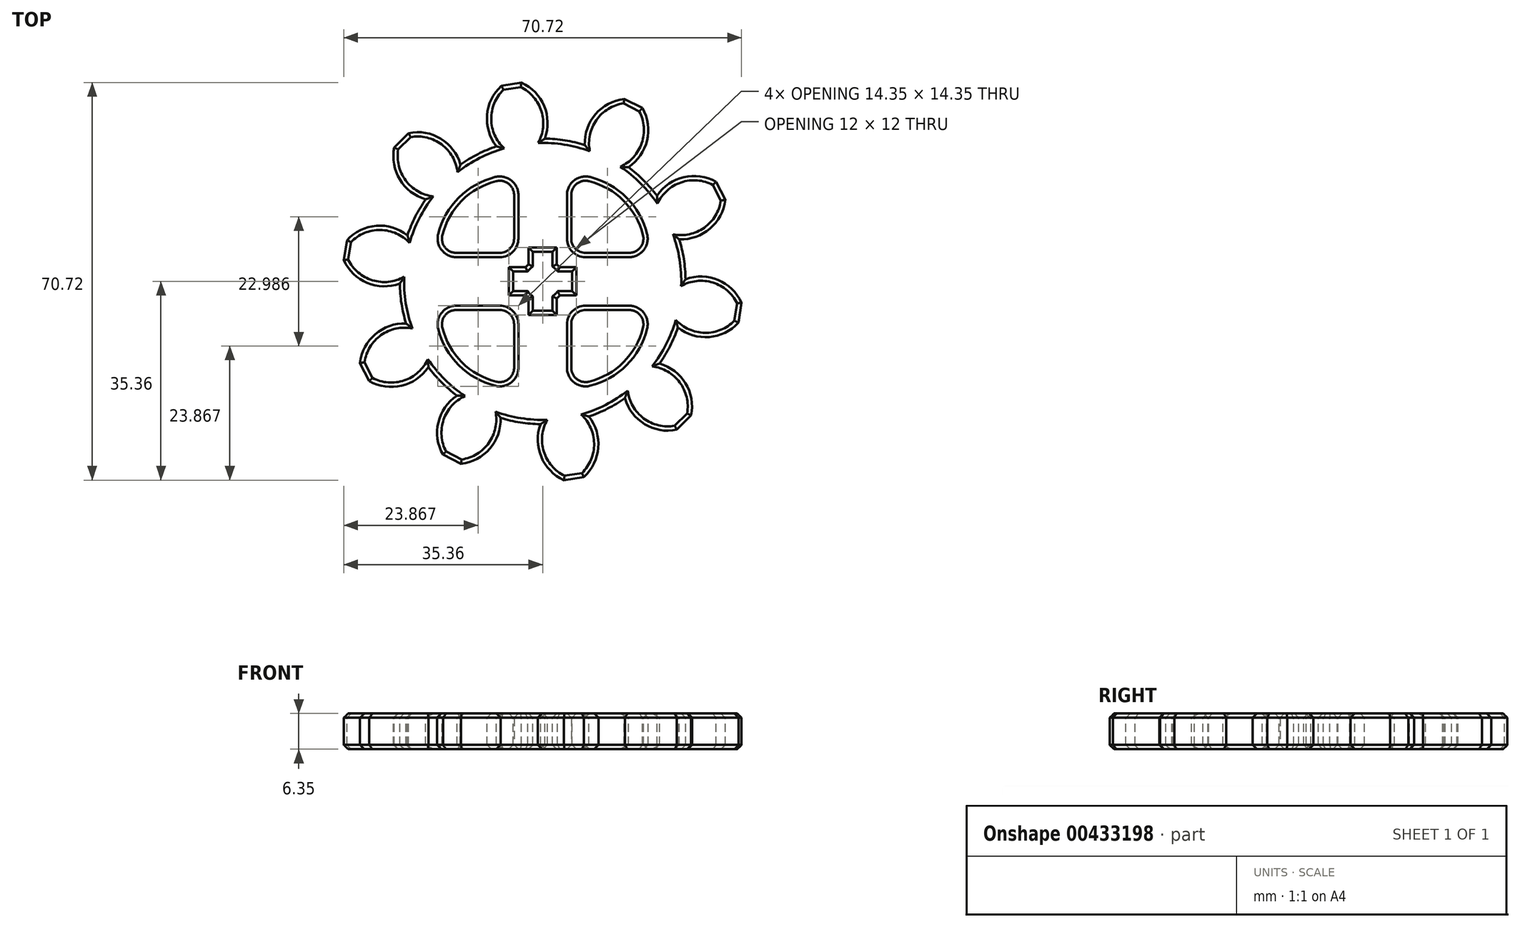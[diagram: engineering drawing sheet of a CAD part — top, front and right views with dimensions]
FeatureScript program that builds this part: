
annotation { "Feature Type Name" : "Feature", "Feature Type Description" : "" }
export const myFeature = defineFeature(function(context is Context, id is Id, definition is map)
    precondition{}
    {
        {
            var Q0;
            Q0=qCreatedBy(makeId("Top.planeOp"),FACE);
            var sketch = newSketch(context, id + "F0", { "sketchPlane" : qUnion([Q0])});
            skCircle(sketch, "E0", {"center": v(0, 0) * mm, "radius": 30.48 * mm, "construction": true});
            skSolve(sketch);
        }
        {
            var Q0;
            Q0=qCreatedBy(makeId("Top.planeOp"),FACE);
            var sketch = newSketch(context, id + "F1", { "sketchPlane" : qUnion([Q0])});
            skCircle(sketch, "E1", {"center": v(0, 0) * mm, "radius": 35.56 * mm, "construction": true});
            skCircle(sketch, "E2", {"center": v(0, 0) * mm, "radius": 31.75 * mm, "construction": true});
            skCircle(sketch, "E3", {"center": v(0, 0) * mm, "radius": 25.4 * mm, "construction": true});
            skLineSegment(sketch, "E4", {"start": v(0, 0) * mm, "end": v(0, 82.3) * mm, "construction": true});
            skLineSegment(sketch, "E5", {"start": v(0, 0) * mm, "end": v(-12.5, 78.88) * mm, "construction": true});
            skLineSegment(sketch, "E6", {"start": v(0, 31.75) * mm, "end": v(-65.71, 31.75) * mm, "construction": true});
            skLineSegment(sketch, "E7", {"start": v(0, 31.75) * mm, "end": v(-58.85, 5.55) * mm, "construction": true});
            skCircle(sketch, "E8", {"center": v(0, 31.75) * mm, "radius": 7.94 * mm, "construction": true});
            skCircle(sketch, "E9", {"center": v(0, 0) * mm, "radius": 29 * mm, "construction": true});
            skCircle(sketch, "E10", {"center": v(-7.06, 28.13) * mm, "radius": 7.94 * mm, "construction": true});
            skArc(sketch, "E11", {"start": v(0.39, 25.4) * mm, "mid": v(0.26, 31.2) * mm, "end": v(-3.78, 35.36) * mm});
            skArc(sketch, "E12.MirrorCS", {"start": v(-8.22, 24.03) * mm, "mid": v(-9.88, 29.59) * mm, "end": v(-7.33, 34.8) * mm});
            skLineSegment(sketch, "E13", {"start": v(-7.33, 34.8) * mm, "end": v(-3.78, 35.36) * mm});
            skArc(sketch, "E14", {"start": v(-8.22, 24.03) * mm, "mid": v(3.97, -25.09) * mm, "end": v(0.39, 25.4) * mm});
            skSolve(sketch);
        }
        {
            var Q0;
            Q0=qSketchRegion(id+"F1",true);
            var Q1;
            Q1=makeQuery(id+"Ffi0VH93psu6soF_0.opExtrude","CAP_FACE",FACE,{"disambiguationData":[OSD([sQuery(id+"F0.wireOp",EDGE,"E0")])],"isStart":true});
            extrude(context, id + "F2", {"entities" : qUnion([Q0]), "oppositeDirection" : true, "endBoundEntityFace" : qUnion([Q1]), "depth" : 6.35 * mm});
        }
        {
            var Q0;
            Q0=makeQuery(id+"F2.opExtrude","SWEPT_BODY",BODY,{"disambiguationData":[OSD([sQuery(id+"F1.wireOp",EDGE,"E11"),sQuery(id+"F1.wireOp",EDGE,"E12.MirrorCS"),sQuery(id+"F1.wireOp",EDGE,"E13"),sQuery(id+"F1.wireOp",EDGE,"ZPE7Z8ba-rLlS-d3gG-Tl0h-fifcE816pJjn")])]});
            var Q1;
            Q1=sQuery(id+"F0.wireOp",EDGE,"E0");
            circularPattern(context, id + "F3", {"operationType" : NewBodyOperationType.ADD, "entities" : qUnion([Q0]), "axis" : qUnion([Q1]), "angle" : 360 * degree, "instanceCount" : 10, "equalSpace" : true});
        }
        {
            var Q0;
            {var subQ0=makeQuery(id+"F2.opExtrude","CAP_FACE",FACE,{"disambiguationData":[OSD([sQuery(id+"F1.wireOp",EDGE,"E11"),sQuery(id+"F1.wireOp",EDGE,"E12.MirrorCS"),sQuery(id+"F1.wireOp",EDGE,"E13"),sQuery(id+"F1.wireOp",EDGE,"ZPE7Z8ba-rLlS-d3gG-Tl0h-fifcE816pJjn")])],"isStart":true});Q0=makeQuery(id+"F3.boolean.opBoolean","MERGE",FACE,{"derivedFrom":[makeQuery(id+"Ffi0VH93psu6soF_0.opExtrude","CAP_FACE",FACE,{"disambiguationData":[OSD([sQuery(id+"F0.wireOp",EDGE,"E0")])],"isStart":false}),subQ0,makeQuery(id+"F3.opPattern","COPY",FACE,{"derivedFrom":subQ0,"instanceName":"1"}),makeQuery(id+"F3.opPattern","COPY",FACE,{"derivedFrom":subQ0,"instanceName":"2"}),makeQuery(id+"F3.opPattern","COPY",FACE,{"derivedFrom":subQ0,"instanceName":"3"}),makeQuery(id+"F3.opPattern","COPY",FACE,{"derivedFrom":subQ0,"instanceName":"4"}),makeQuery(id+"F3.opPattern","COPY",FACE,{"derivedFrom":subQ0,"instanceName":"5"}),makeQuery(id+"F3.opPattern","COPY",FACE,{"derivedFrom":subQ0,"instanceName":"6"}),makeQuery(id+"F3.opPattern","COPY",FACE,{"derivedFrom":subQ0,"instanceName":"7"}),makeQuery(id+"F3.opPattern","COPY",FACE,{"derivedFrom":subQ0,"instanceName":"8"}),makeQuery(id+"F3.opPattern","COPY",FACE,{"derivedFrom":subQ0,"instanceName":"9"}),makeQuery(id+"F3.opPattern","COPY",FACE,{"derivedFrom":subQ0,"instanceName":"10"}),makeQuery(id+"F3.opPattern","COPY",FACE,{"derivedFrom":subQ0,"instanceName":"11"}),makeQuery(id+"F3.opPattern","COPY",FACE,{"derivedFrom":subQ0,"instanceName":"12"}),makeQuery(id+"F3.opPattern","COPY",FACE,{"derivedFrom":subQ0,"instanceName":"13"}),makeQuery(id+"F3.opPattern","COPY",FACE,{"derivedFrom":subQ0,"instanceName":"14"})]});}
            var sketch = newSketch(context, id + "F4", { "sketchPlane" : qUnion([Q0])});
            skLineSegment(sketch, "E15", {"start": v(-5.08, 5.08) * mm, "end": v(-18.22, 5.08) * mm});
            skLineSegment(sketch, "E16", {"start": v(-5.08, 5.08) * mm, "end": v(-5.08, 18.22) * mm});
            skArc(sketch, "E17", {"start": v(-5.08, 18.22) * mm, "mid": v(-14.37, 14.37) * mm, "end": v(-18.22, 5.08) * mm});
            skArc(sketch, "E18.1.0", {"start": v(-18.22, -5.08) * mm, "mid": v(-14.37, -14.37) * mm, "end": v(-5.08, -18.22) * mm});
            skLineSegment(sketch, "E18.1.1", {"start": v(-5.08, -5.08) * mm, "end": v(-18.22, -5.08) * mm});
            skLineSegment(sketch, "E18.1.2", {"start": v(-5.08, -5.08) * mm, "end": v(-5.08, -18.22) * mm});
            skArc(sketch, "E18.2.0", {"start": v(5.08, -18.22) * mm, "mid": v(14.37, -14.37) * mm, "end": v(18.22, -5.08) * mm});
            skLineSegment(sketch, "E18.2.1", {"start": v(5.08, -5.08) * mm, "end": v(5.08, -18.22) * mm});
            skLineSegment(sketch, "E18.2.2", {"start": v(5.08, -5.08) * mm, "end": v(18.22, -5.08) * mm});
            skArc(sketch, "E18.3.0", {"start": v(18.22, 5.08) * mm, "mid": v(14.37, 14.37) * mm, "end": v(5.08, 18.22) * mm});
            skLineSegment(sketch, "E18.3.1", {"start": v(5.08, 5.08) * mm, "end": v(18.22, 5.08) * mm});
            skLineSegment(sketch, "E18.3.2", {"start": v(5.08, 5.08) * mm, "end": v(5.08, 18.22) * mm});
            skPoint(sketch, "E18.center", {"position": v(0, 0) * mm});
            skSolve(sketch);
        }
        {
            var Q0;
            Q0=qSketchRegion(id+"F4",true);
            extrude(context, id + "F5", {"entities" : qUnion([Q0]), "operationType" : NewBodyOperationType.REMOVE, "endBound" : BoundingType.THROUGH_ALL, "oppositeDirection" : true, "depth" : 25.4 * mm});
        }
        {
            var Q0;
            {var subQ0=makeQuery(id+"F2.opExtrude","CAP_FACE",FACE,{"disambiguationData":[OSD([sQuery(id+"F1.wireOp",EDGE,"E11"),sQuery(id+"F1.wireOp",EDGE,"E12.MirrorCS"),sQuery(id+"F1.wireOp",EDGE,"E13"),sQuery(id+"F1.wireOp",EDGE,"E14")])],"isStart":true});Q0=makeQuery(id+"F3.boolean.opBoolean","MERGE",FACE,{"derivedFrom":[subQ0,makeQuery(id+"F3.opPattern","COPY",FACE,{"derivedFrom":subQ0,"instanceName":"1"}),makeQuery(id+"F3.opPattern","COPY",FACE,{"derivedFrom":subQ0,"instanceName":"2"}),makeQuery(id+"F3.opPattern","COPY",FACE,{"derivedFrom":subQ0,"instanceName":"3"}),makeQuery(id+"F3.opPattern","COPY",FACE,{"derivedFrom":subQ0,"instanceName":"4"}),makeQuery(id+"F3.opPattern","COPY",FACE,{"derivedFrom":subQ0,"instanceName":"5"}),makeQuery(id+"F3.opPattern","COPY",FACE,{"derivedFrom":subQ0,"instanceName":"6"}),makeQuery(id+"F3.opPattern","COPY",FACE,{"derivedFrom":subQ0,"instanceName":"7"}),makeQuery(id+"F3.opPattern","COPY",FACE,{"derivedFrom":subQ0,"instanceName":"8"}),makeQuery(id+"F3.opPattern","COPY",FACE,{"derivedFrom":subQ0,"instanceName":"9"})]});}
            var sketch = newSketch(context, id + "F6", { "sketchPlane" : qUnion([Q0])});
            skCircle(sketch, "E19", {"center": v(0, 0) * mm, "radius": 3.18 * mm});
            skSolve(sketch);
        }
        {
            var Q0;
            Q0=qSketchRegion(id+"F6",true);
            extrude(context, id + "F7", {"entities" : qUnion([Q0]), "operationType" : NewBodyOperationType.REMOVE, "oppositeDirection" : true, "depth" : 7.62 * mm, "offsetDistance" : 25.4 * mm});
        }
        {
            var Q0;
            {var subQ0=makeQuery(id+"F2.opExtrude","CAP_FACE",FACE,{"disambiguationData":[OSD([sQuery(id+"F1.wireOp",EDGE,"E11"),sQuery(id+"F1.wireOp",EDGE,"E12.MirrorCS"),sQuery(id+"F1.wireOp",EDGE,"E13"),sQuery(id+"F1.wireOp",EDGE,"E14")])],"isStart":true});Q0=makeQuery(id+"F3.boolean.opBoolean","MERGE",FACE,{"derivedFrom":[subQ0,makeQuery(id+"F3.opPattern","COPY",FACE,{"derivedFrom":subQ0,"instanceName":"1"}),makeQuery(id+"F3.opPattern","COPY",FACE,{"derivedFrom":subQ0,"instanceName":"2"}),makeQuery(id+"F3.opPattern","COPY",FACE,{"derivedFrom":subQ0,"instanceName":"3"}),makeQuery(id+"F3.opPattern","COPY",FACE,{"derivedFrom":subQ0,"instanceName":"4"}),makeQuery(id+"F3.opPattern","COPY",FACE,{"derivedFrom":subQ0,"instanceName":"5"}),makeQuery(id+"F3.opPattern","COPY",FACE,{"derivedFrom":subQ0,"instanceName":"6"}),makeQuery(id+"F3.opPattern","COPY",FACE,{"derivedFrom":subQ0,"instanceName":"7"}),makeQuery(id+"F3.opPattern","COPY",FACE,{"derivedFrom":subQ0,"instanceName":"8"}),makeQuery(id+"F3.opPattern","COPY",FACE,{"derivedFrom":subQ0,"instanceName":"9"})]});}
            var sketch = newSketch(context, id + "F8", { "sketchPlane" : qUnion([Q0])});
            skLineSegment(sketch, "E20.bottom", {"start": v(-1.75, 5.24) * mm, "end": v(1.75, 5.24) * mm});
            skLineSegment(sketch, "E20.top", {"start": v(-1.75, -5.24) * mm, "end": v(1.75, -5.24) * mm});
            skLineSegment(sketch, "E20.left", {"start": v(-1.75, 5.24) * mm, "end": v(-1.75, 1.75) * mm});
            skLineSegment(sketch, "E20.right", {"start": v(1.75, 5.24) * mm, "end": v(1.75, 1.75) * mm});
            skPoint(sketch, "E20.middle", {"position": v(0, 0) * mm});
            skLineSegment(sketch, "E21.bottom", {"start": v(5.24, -1.75) * mm, "end": v(1.75, -1.75) * mm});
            skLineSegment(sketch, "E21.top", {"start": v(5.24, 1.75) * mm, "end": v(1.75, 1.75) * mm});
            skLineSegment(sketch, "E21.left", {"start": v(5.24, -1.75) * mm, "end": v(5.24, 1.75) * mm});
            skLineSegment(sketch, "E21.right", {"start": v(-5.24, -1.75) * mm, "end": v(-5.24, 1.75) * mm});
            skLineSegment(sketch, "E22.trimOffspring", {"start": v(-1.75, 1.75) * mm, "end": v(-5.24, 1.75) * mm});
            skLineSegment(sketch, "E23.trimOffspring", {"start": v(-1.75, -1.75) * mm, "end": v(-1.75, -5.24) * mm});
            skLineSegment(sketch, "E24.trimOffspring", {"start": v(-1.75, -1.75) * mm, "end": v(-5.24, -1.75) * mm});
            skLineSegment(sketch, "E25.trimOffspring", {"start": v(1.75, -1.75) * mm, "end": v(1.75, -5.24) * mm});
            skSolve(sketch);
        }
        {
            var Q0;
            Q0 = qSketchRegion(id + "F8", true);
            extrude(context, id + "F9", {"entities" : qUnion([Q0]), "operationType" : NewBodyOperationType.REMOVE, "endBound" : BoundingType.THROUGH_ALL, "oppositeDirection" : true, "depth" : 25.4 * mm, "offsetDistance" : 25.4 * mm});
        }
        {
            var Q0;
            Q0=makeQuery(id+"F5.boolean.opBoolean","COPY",EDGE,{"derivedFrom":makeQuery(id+"F5.opExtrude","SWEPT_EDGE",EDGE,{"disambiguationData":[OSD([sQuery(id+"F4.wireOp",EDGE,"E16"),sQuery(id+"F4.wireOp",EDGE,"E17")])]})});
            var Q1;
            Q1=makeQuery(id+"F5.boolean.opBoolean","COPY",EDGE,{"derivedFrom":makeQuery(id+"F5.opExtrude","SWEPT_EDGE",EDGE,{"disambiguationData":[OSD([sQuery(id+"F4.wireOp",EDGE,"E15"),sQuery(id+"F4.wireOp",EDGE,"E16")])]})});
            var Q2;
            Q2=makeQuery(id+"F5.boolean.opBoolean","COPY",EDGE,{"derivedFrom":makeQuery(id+"F5.opExtrude","SWEPT_EDGE",EDGE,{"disambiguationData":[OSD([sQuery(id+"F4.wireOp",EDGE,"E15"),sQuery(id+"F4.wireOp",EDGE,"E17")])]})});
            var Q3;
            Q3=makeQuery(id+"F5.boolean.opBoolean","COPY",EDGE,{"derivedFrom":makeQuery(id+"F5.opExtrude","SWEPT_EDGE",EDGE,{"disambiguationData":[OSD([sQuery(id+"F4.wireOp",EDGE,"E18.3.1"),sQuery(id+"F4.wireOp",EDGE,"E18.3.2")])]})});
            var Q4;
            Q4=makeQuery(id+"F5.boolean.opBoolean","COPY",EDGE,{"derivedFrom":makeQuery(id+"F5.opExtrude","SWEPT_EDGE",EDGE,{"disambiguationData":[OSD([sQuery(id+"F4.wireOp",EDGE,"E18.3.0"),sQuery(id+"F4.wireOp",EDGE,"E18.3.2")])]})});
            var Q5;
            Q5=makeQuery(id+"F5.boolean.opBoolean","COPY",EDGE,{"derivedFrom":makeQuery(id+"F5.opExtrude","SWEPT_EDGE",EDGE,{"disambiguationData":[OSD([sQuery(id+"F4.wireOp",EDGE,"E18.3.0"),sQuery(id+"F4.wireOp",EDGE,"E18.3.1")])]})});
            var Q6;
            Q6=makeQuery(id+"F5.boolean.opBoolean","COPY",EDGE,{"derivedFrom":makeQuery(id+"F5.opExtrude","SWEPT_EDGE",EDGE,{"disambiguationData":[OSD([sQuery(id+"F4.wireOp",EDGE,"E18.1.0"),sQuery(id+"F4.wireOp",EDGE,"E18.1.2")])]})});
            var Q7;
            Q7=makeQuery(id+"F5.boolean.opBoolean","COPY",EDGE,{"derivedFrom":makeQuery(id+"F5.opExtrude","SWEPT_EDGE",EDGE,{"disambiguationData":[OSD([sQuery(id+"F4.wireOp",EDGE,"E18.1.0"),sQuery(id+"F4.wireOp",EDGE,"E18.1.1")])]})});
            var Q8;
            Q8=makeQuery(id+"F5.boolean.opBoolean","COPY",EDGE,{"derivedFrom":makeQuery(id+"F5.opExtrude","SWEPT_EDGE",EDGE,{"disambiguationData":[OSD([sQuery(id+"F4.wireOp",EDGE,"E18.1.1"),sQuery(id+"F4.wireOp",EDGE,"E18.1.2")])]})});
            var Q9;
            Q9=makeQuery(id+"F5.boolean.opBoolean","COPY",EDGE,{"derivedFrom":makeQuery(id+"F5.opExtrude","SWEPT_EDGE",EDGE,{"disambiguationData":[OSD([sQuery(id+"F4.wireOp",EDGE,"E18.2.0"),sQuery(id+"F4.wireOp",EDGE,"E18.2.2")])]})});
            var Q10;
            Q10=makeQuery(id+"F5.boolean.opBoolean","COPY",EDGE,{"derivedFrom":makeQuery(id+"F5.opExtrude","SWEPT_EDGE",EDGE,{"disambiguationData":[OSD([sQuery(id+"F4.wireOp",EDGE,"E18.2.0"),sQuery(id+"F4.wireOp",EDGE,"E18.2.1")])]})});
            var Q11;
            Q11=makeQuery(id+"F5.boolean.opBoolean","COPY",EDGE,{"derivedFrom":makeQuery(id+"F5.opExtrude","SWEPT_EDGE",EDGE,{"disambiguationData":[OSD([sQuery(id+"F4.wireOp",EDGE,"E18.2.1"),sQuery(id+"F4.wireOp",EDGE,"E18.2.2")])]})});
            fillet(context, id + "F10", {"entities" : qUnion([Q0, Q1, Q2, Q3, Q4, Q5, Q6, Q7, Q8, Q9, Q10, Q11]), "radius" : 2.54 * mm, "tangentPropagation" : true, "allowEdgeOverflow" : false});
        }
        {
            var Q0;
            {var subQ0=makeQuery(id+"F2.opExtrude","CAP_FACE",FACE,{"disambiguationData":[OSD([sQuery(id+"F1.wireOp",EDGE,"E11"),sQuery(id+"F1.wireOp",EDGE,"E12.MirrorCS"),sQuery(id+"F1.wireOp",EDGE,"E13"),sQuery(id+"F1.wireOp",EDGE,"E14")])],"isStart":true});Q0=makeQuery(id+"F3.boolean.opBoolean","MERGE",FACE,{"derivedFrom":[subQ0,makeQuery(id+"F3.opPattern","COPY",FACE,{"derivedFrom":subQ0,"instanceName":"1"}),makeQuery(id+"F3.opPattern","COPY",FACE,{"derivedFrom":subQ0,"instanceName":"2"}),makeQuery(id+"F3.opPattern","COPY",FACE,{"derivedFrom":subQ0,"instanceName":"3"}),makeQuery(id+"F3.opPattern","COPY",FACE,{"derivedFrom":subQ0,"instanceName":"4"}),makeQuery(id+"F3.opPattern","COPY",FACE,{"derivedFrom":subQ0,"instanceName":"5"}),makeQuery(id+"F3.opPattern","COPY",FACE,{"derivedFrom":subQ0,"instanceName":"6"}),makeQuery(id+"F3.opPattern","COPY",FACE,{"derivedFrom":subQ0,"instanceName":"7"}),makeQuery(id+"F3.opPattern","COPY",FACE,{"derivedFrom":subQ0,"instanceName":"8"}),makeQuery(id+"F3.opPattern","COPY",FACE,{"derivedFrom":subQ0,"instanceName":"9"})]});}
            var Q1;
            {var subQ0=makeQuery(id+"F2.opExtrude","CAP_FACE",FACE,{"disambiguationData":[OSD([sQuery(id+"F1.wireOp",EDGE,"E11"),sQuery(id+"F1.wireOp",EDGE,"E12.MirrorCS"),sQuery(id+"F1.wireOp",EDGE,"E13"),sQuery(id+"F1.wireOp",EDGE,"E14")])],"isStart":false});Q1=makeQuery(id+"F3.boolean.opBoolean","MERGE",FACE,{"derivedFrom":[subQ0,makeQuery(id+"F3.opPattern","COPY",FACE,{"derivedFrom":subQ0,"instanceName":"1"}),makeQuery(id+"F3.opPattern","COPY",FACE,{"derivedFrom":subQ0,"instanceName":"2"}),makeQuery(id+"F3.opPattern","COPY",FACE,{"derivedFrom":subQ0,"instanceName":"3"}),makeQuery(id+"F3.opPattern","COPY",FACE,{"derivedFrom":subQ0,"instanceName":"4"}),makeQuery(id+"F3.opPattern","COPY",FACE,{"derivedFrom":subQ0,"instanceName":"5"}),makeQuery(id+"F3.opPattern","COPY",FACE,{"derivedFrom":subQ0,"instanceName":"6"}),makeQuery(id+"F3.opPattern","COPY",FACE,{"derivedFrom":subQ0,"instanceName":"7"}),makeQuery(id+"F3.opPattern","COPY",FACE,{"derivedFrom":subQ0,"instanceName":"8"}),makeQuery(id+"F3.opPattern","COPY",FACE,{"derivedFrom":subQ0,"instanceName":"9"})]});}
            chamfer(context, id + "F11", {"entities" : qUnion([Q0, Q1]), "width" : 0.76 * mm, "tangentPropagation" : true});
        }
    });
